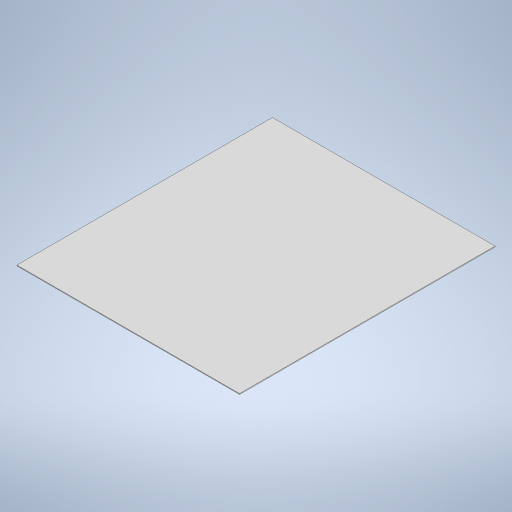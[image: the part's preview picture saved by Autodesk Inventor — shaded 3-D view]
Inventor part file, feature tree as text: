
AUTODESK INVENTOR PART (.ipt)
format: ipt  version: 2023.1 (Build 271208000, 208)  size: 201,728 bytes
history: native  units: in
note: dims shown in document units (in); Inventor stores cm internally (conversion verified against a paired STEP export)
features: extrude x1, sketch x1
ambient origin geometry x8: Origin, YZ Plane, XZ Plane, XY Plane, X Axis, Y Axis, Z Axis, Center Point
bodies: Solid1 (feature_tree)
feature tree (2):
  extrude  "Extrusion1"  Depth=17.3228in
  sketch  "Sketch1"  dims[d1=19.8819in d2=17.3228in d3=0.063in d4=0.0in]
